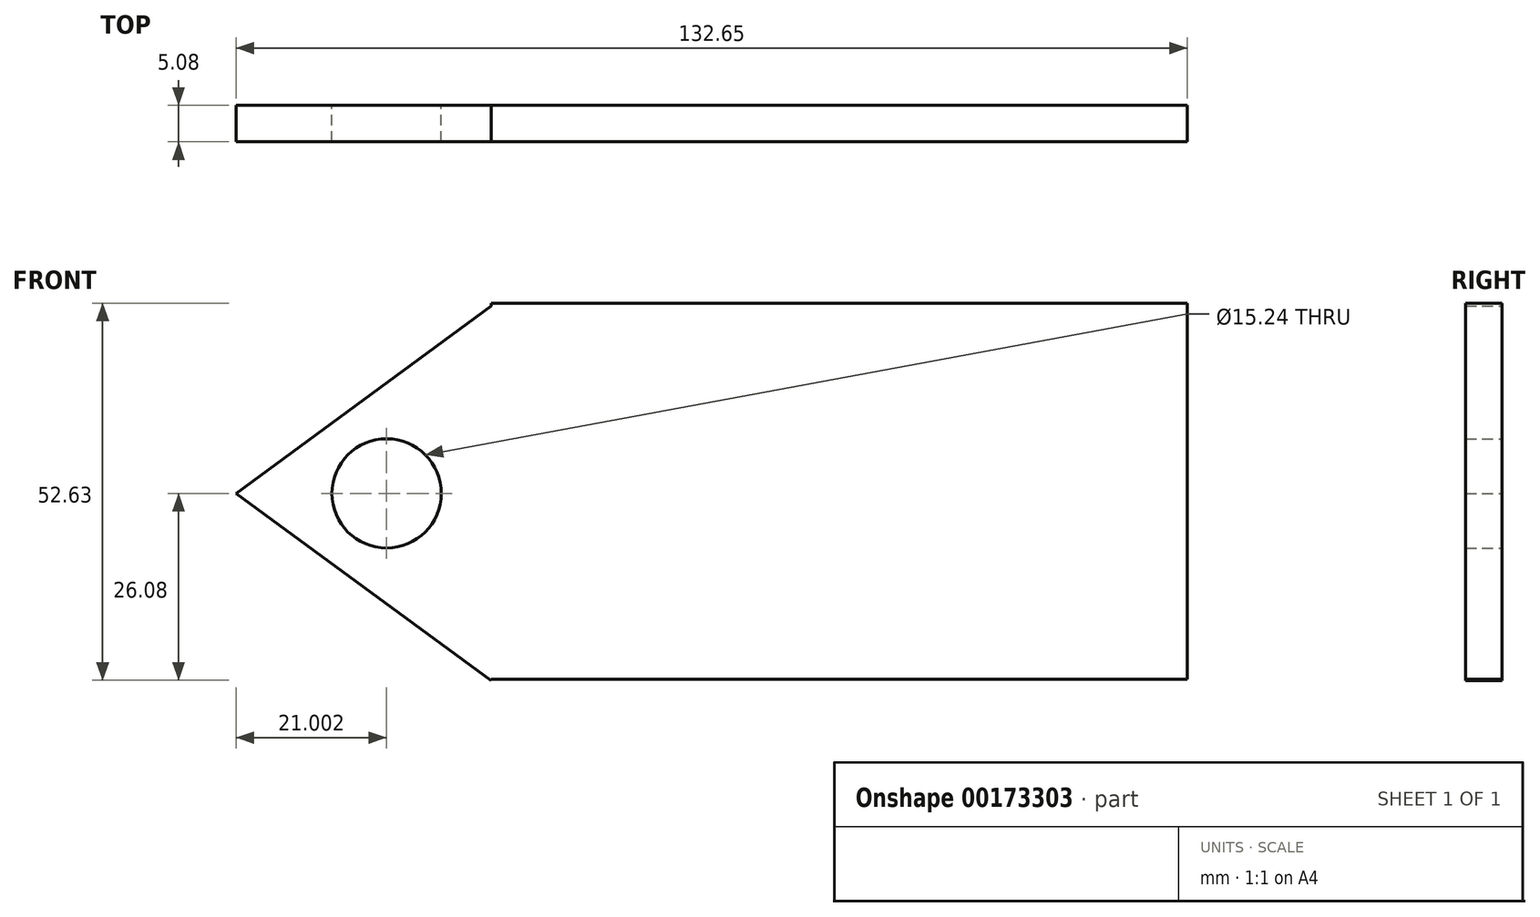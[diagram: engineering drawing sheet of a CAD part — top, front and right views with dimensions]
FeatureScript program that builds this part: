
annotation { "Feature Type Name" : "Feature", "Feature Type Description" : "" }
export const myFeature = defineFeature(function(context is Context, id is Id, definition is map)
    precondition{}
    {
        {
            var Q0;
            Q0=qCreatedBy(makeId("Front.planeOp"),FACE);
            var sketch = newSketch(context, id + "F0", { "sketchPlane" : qUnion([Q0])});
            skLineSegment(sketch, "E0.bottom", {"start": v(-30.42, 26.55) * mm, "end": v(66.65, 26.55) * mm});
            skLineSegment(sketch, "E0.top", {"start": v(-30.42, -25.9) * mm, "end": v(66.65, -25.9) * mm});
            skLineSegment(sketch, "E0.left", {"start": v(-30.42, 26.55) * mm, "end": v(-30.42, -25.9) * mm});
            skLineSegment(sketch, "E0.right", {"start": v(66.65, 26.55) * mm, "end": v(66.65, -25.9) * mm});
            skSolve(sketch);
        }
        {
            var Q0;
            Q0=makeQuery(id+"F0.imprint","IMPRINT",FACE,{"disambiguationData":[TD([[makeQuery(id+"F0.imprint","IMPRINT",EDGE,{"derivedFrom":sQuery(id+"F0.wireOp",EDGE,"E0.bottom")}),-1.0]])]});
            extrude(context, id + "F1", {"entities" : qUnion([Q0]), "depth" : 5.08 * mm});
        }
        {
            var Q0;
            Q0=qCreatedBy(makeId("Front.planeOp"),FACE);
            var sketch = newSketch(context, id + "F2", { "sketchPlane" : qUnion([Q0])});
            skLineSegment(sketch, "E1", {"start": v(-30.42, 26.16) * mm, "end": v(-66, 0) * mm});
            skLineSegment(sketch, "E2", {"start": v(-66, 0) * mm, "end": v(-30.42, -26.08) * mm});
            skLineSegment(sketch, "E3", {"start": v(-30.42, -26.08) * mm, "end": v(-30.42, 26.16) * mm});
            skSolve(sketch);
        }
        {
            var Q0;
            Q0 = qSketchRegion(id + "F2", true);
            extrude(context, id + "F3", {"entities" : qUnion([Q0]), "operationType" : NewBodyOperationType.ADD, "depth" : 5.08 * mm});
        }
        {
            var Q0;
            Q0=qCreatedBy(makeId("Front.planeOp"),FACE);
            var sketch = newSketch(context, id + "F4", { "sketchPlane" : qUnion([Q0])});
            skCircle(sketch, "E4", {"center": v(-45, 0) * mm, "radius": 6.27 * mm});
            skSolve(sketch);
        }
        {
            var Q0;
            Q0=sQuery(id+"F4.wireOp",VERTEX,"E4.center");
            var Q1;
            Q1=makeQuery(id+"F1.opExtrude","SWEPT_BODY",BODY,{"disambiguationData":[OSD([sQuery(id+"F0.wireOp",EDGE,"E0.bottom"),sQuery(id+"F0.wireOp",EDGE,"E0.top"),sQuery(id+"F0.wireOp",EDGE,"E0.left"),sQuery(id+"F0.wireOp",EDGE,"E0.right")])]});
            hole(context, id + "F5", {"style" : HoleStyle.SIMPLE, "endStyle" : HoleEndStyle.THROUGH, "oppositeDirection" : true, "holeDiameter" : 15.24 * mm, "locations" : qUnion([Q0]), "scope" : qUnion([Q1]), "isTappedThrough" : true});
        }
    });
